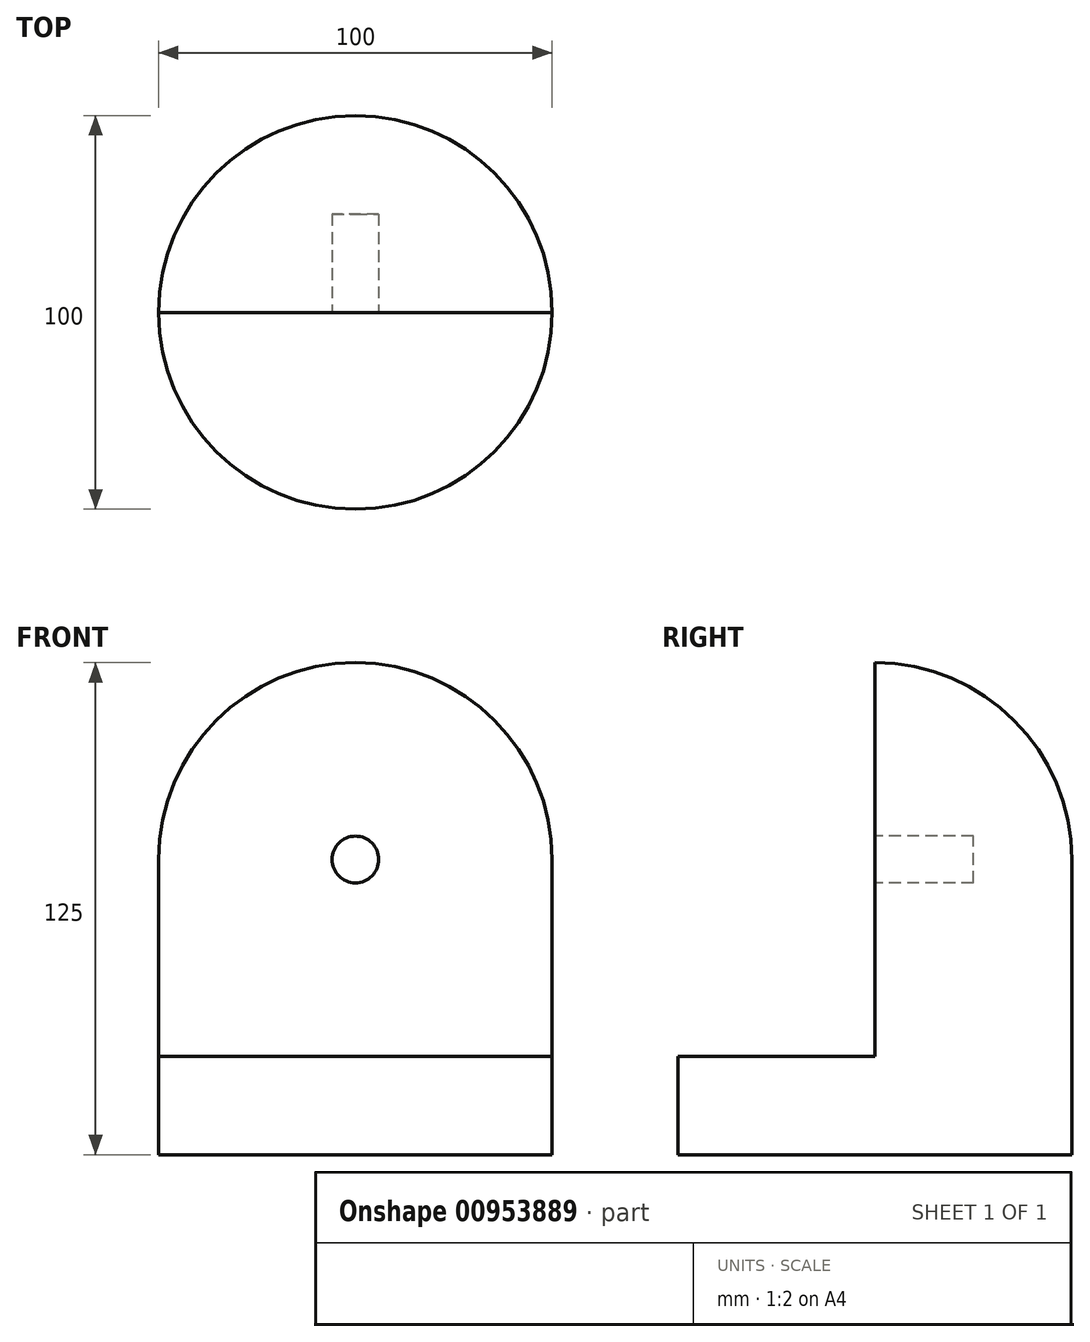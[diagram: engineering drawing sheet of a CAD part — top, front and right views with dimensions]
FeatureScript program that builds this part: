
annotation { "Feature Type Name" : "Feature", "Feature Type Description" : "" }
export const myFeature = defineFeature(function(context is Context, id is Id, definition is map)
    precondition{}
    {
        {
            var Q0;
            Q0=qCreatedBy(makeId("Top.planeOp"),FACE);
            var sketch = newSketch(context, id + "F0", { "sketchPlane" : qUnion([Q0])});
            skCircle(sketch, "E0", {"center": v(0, 0) * mm, "radius": 50 * mm});
            skSolve(sketch);
        }
        {
            var Q0;
            Q0=makeQuery(id+"F0.imprint","IMPRINT",FACE,{"disambiguationData":[TD([[makeQuery(id+"F0.imprint","IMPRINT",EDGE,{"derivedFrom":sQuery(id+"F0.wireOp",EDGE,"E0")}),1.0]])]});
            extrude(context, id + "F1", {"entities" : qUnion([Q0]), "depth" : 25 * mm, "offsetDistance" : 25 * mm});
        }
        {
            var Q0;
            Q0=makeQuery(id+"F1.opExtrude","CAP_FACE",FACE,{"disambiguationData":[OSD([sQuery(id+"F0.wireOp",EDGE,"E0")])],"isStart":false});
            var sketch = newSketch(context, id + "F2", { "sketchPlane" : qUnion([Q0])});
            skArc(sketch, "E1", {"start": v(50, 0) * mm, "mid": v(0, 50) * mm, "end": v(-50, 0) * mm});
            skLineSegment(sketch, "E2", {"start": v(-50, 0) * mm, "end": v(50, 0) * mm});
            skSolve(sketch);
        }
        {
            var Q0;
            Q0=makeQuery(id+"F2.imprint","IMPRINT",FACE,{"disambiguationData":[TD([[makeQuery(id+"F2.imprint","IMPRINT",EDGE,{"derivedFrom":sQuery(id+"F2.wireOp",EDGE,"E1")}),1.0]])]});
            extrude(context, id + "F3", {"entities" : qUnion([Q0]), "operationType" : NewBodyOperationType.ADD, "depth" : 50 * mm, "offsetDistance" : 25 * mm});
        }
        {
            var Q0;
            Q0=makeQuery(id+"F3.opExtrude","SWEPT_FACE",FACE,{"disambiguationData":[OSD([sQuery(id+"F2.wireOp",EDGE,"E2")])]});
            var sketch = newSketch(context, id + "F4", { "sketchPlane" : qUnion([Q0])});
            skArc(sketch, "E3", {"start": v(50, 75) * mm, "mid": v(0, 125) * mm, "end": v(-50, 75) * mm});
            skLineSegment(sketch, "E4", {"start": v(-50, 75) * mm, "end": v(50, 75) * mm});
            skSolve(sketch);
        }
        {
            var Q0;
            Q0=qCreatedBy(makeId("Right.planeOp"),FACE);
            var sketch = newSketch(context, id + "F5", { "sketchPlane" : qUnion([Q0])});
            skArc(sketch, "E5", {"start": v(49.73, 75) * mm, "mid": v(35.16, 110.16) * mm, "end": v(0, 124.73) * mm});
            skLineSegment(sketch, "E6", {"start": v(0, 75) * mm, "end": v(49.73, 75) * mm});
            skLineSegment(sketch, "E7", {"start": v(0, 124.73) * mm, "end": v(0, 75) * mm});
            skSolve(sketch);
        }
        {
            var Q0;
            Q0=sQuery(id+"F5.wireOp",EDGE,"E5");
            var Q2;
            Q2=makeQuery(id+"F4.imprint","IMPRINT",FACE,{"disambiguationData":[TD([[makeQuery(id+"F4.imprint","IMPRINT",EDGE,{"derivedFrom":sQuery(id+"F4.wireOp",EDGE,"E3")}),1.0]])]});
            var Q3;
            Q3=makeQuery(id+"F3.opExtrude","CAP_FACE",FACE,{"disambiguationData":[OSD([sQuery(id+"F2.wireOp",EDGE,"E1"),sQuery(id+"F2.wireOp",EDGE,"E2")])],"isStart":false});
            var Q4;
            Q4=sQuery(id+"F5.wireOp",EDGE,"E5");
            loft(context, id + "F6", {"operationType" : NewBodyOperationType.ADD, "addSections" : true, "spine" : qUnion([Q0]), "sectionCount" : 5, "sheetProfilesArray" : [{ "sheetProfileEntities" : qUnion([Q2]) }, { "sheetProfileEntities" : qUnion([Q3]) }], "guidesArray" : [{ "guideEntities" : qUnion([Q4]), "guideDerivativeType" : LoftGuideDerivativeType.DEFAULT, "guideDerivativeMagnitude" : 1 }]});
        }
        {
            var Q0;
            Q0=makeQuery(id+"F6.boolean.opBoolean","MERGE",FACE,{"derivedFrom":[makeQuery(id+"F3.opExtrude","SWEPT_FACE",FACE,{"disambiguationData":[OSD([sQuery(id+"F2.wireOp",EDGE,"E2")])]}),makeQuery(id+"F6.opLoft","CAP_FACE",FACE,{"disambiguationData":[OSD([makeQuery(id+"F4.imprint","IMPRINT",FACE,{"disambiguationData":[TD([[makeQuery(id+"F4.imprint","IMPRINT",EDGE,{"derivedFrom":sQuery(id+"F4.wireOp",EDGE,"E3")}),1.0]])]})])],"isStart":true})]});
            var sketch = newSketch(context, id + "F7", { "sketchPlane" : qUnion([Q0])});
            skCircle(sketch, "E8", {"center": v(0, 75) * mm, "radius": 5.94 * mm});
            skSolve(sketch);
        }
        {
            var Q0;
            Q0=makeQuery(id+"F7.imprint","IMPRINT",FACE,{"disambiguationData":[TD([[makeQuery(id+"F7.imprint","IMPRINT",EDGE,{"derivedFrom":sQuery(id+"F7.wireOp",EDGE,"E8")}),1.0]])]});
            var Q1;
            Q1=sQuery(id+"F7.wireOp",EDGE,"E8");
            extrude(context, id + "F8", {"entities" : qUnion([Q0]), "operationType" : NewBodyOperationType.REMOVE, "surfaceEntities" : qUnion([Q1]), "oppositeDirection" : true, "depth" : 25 * mm, "offsetDistance" : 25 * mm});
        }
    });
